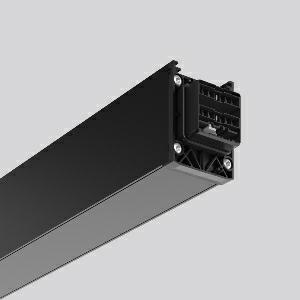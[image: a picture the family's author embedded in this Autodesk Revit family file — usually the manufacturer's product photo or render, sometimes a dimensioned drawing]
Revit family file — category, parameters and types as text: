
# Revit family: linedo_2_3m_00_0000_952300_003_700_900_637d
name_source: partatom
category: Lighting Fixtures
units: mm (PartAtom-declared; Revit-internal decimal feet)

## family parameters
Cut with Voids When Loaded = No
Host = Face
Light Source = No
Part Type = Normal
Room Calculation Point = No
Round Connector Dimension = Use Diameter
Shared = No

## types (1)
- LINEDO_2,3m_00_0000
    Apparent Load = 0 VA
    Default Elevation = 1800 mm
    Description = Series: LINEDO
Rapid-installation complete module for universal use as a continuous line luminaire. Blank module. System profile made of aluminium extrusion profile, powder-coated. Cover made of plastic, surface like housing. Simple, tool-free installation of system profiles using separate accessories for cable, chain or ceiling suspension. Tool-free connection and mechanical connectors to secure. Please order supply module, connection and mounting accessories separately. Luminaire with limited surface temperature in accordance with EN  60598-2-24 for use in environments in which a deposit of non-conductive dust on the luminaire can be expected. 
Colour: deep black, matt (RAL 9005)
Length: 2310 mm
Width: 58 mm
Height: 76 mm
Weight: 4 kg
Type of Installation: Ceiling mounting, Suspension cable/chain
    Height = 76 mm
    Lamp = 0 x
    Length = 2291 mm
    Luminous efficacy = 0 lm/W
    Manufacturer = RZB
    ModVariant = No
    Model = 952300.003.700.900
    Mounting Place = Ceiling
    Mounting Type = Surface mounted, Pendant
    Number of Poles = 1
    OnlyDefault = Yes
    Power Factor = 1
    Product Name = LINEDO_2,3m_00_0000
    Product group = Continuous line luminaire system Linedo IP 54
    ProductGroupID = 314
    Protection Class = Protection class I
    Protection Degree = IP 54
    RLX_Detail_Level = 1
    RLX_Emergency_Light_Flux = 0 lm
    RLX_Emergency_Type = 0
    RLX_Emergency_Type_DB = No
    RlxData = <blob elided: 34161 chars, md5=8a0f883b>
    Standby Power = 0 W
    System Light Flux = 0 lm
    System Power = 0 W
    Type Comments = Product without accessories
    Type Image = 954500.003.400.900.jpg
    URL = http://relux.com
    VarID = ---
    Voltage = 230 V
    Voltage Range = 220-240 V
    Weight = 0.00 kg
    Width = 58 mm

## geometry (parser evidence)
native form markers: Blend x4, Sweep x10
no freeform markers — native parametric forms only
